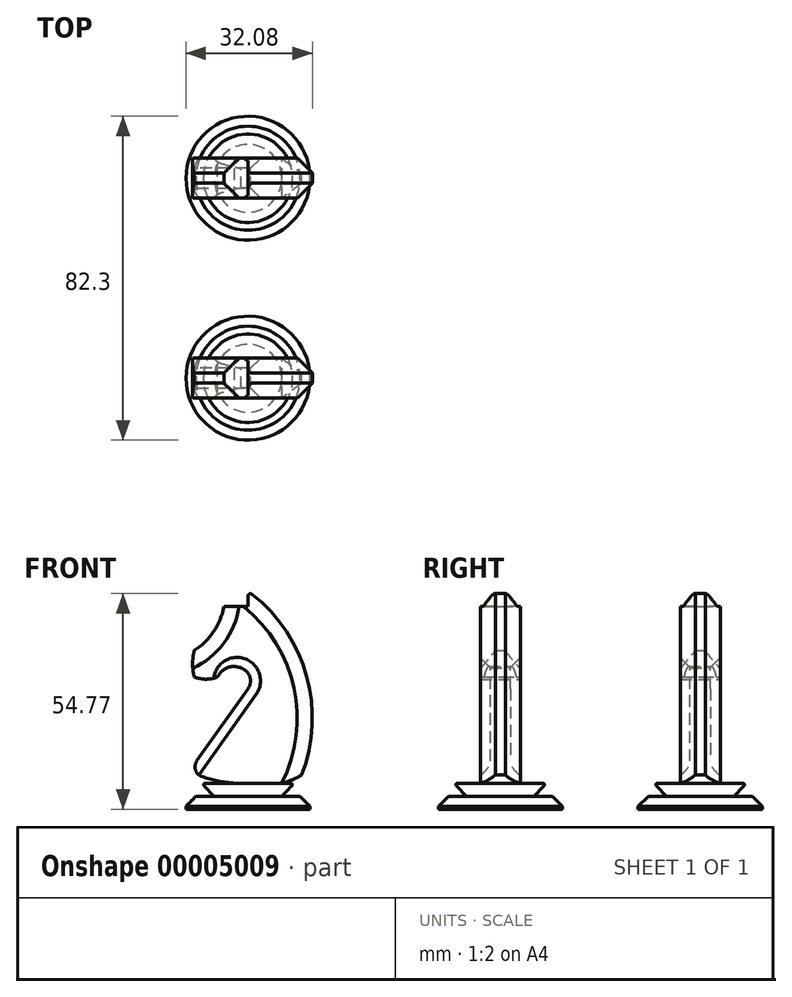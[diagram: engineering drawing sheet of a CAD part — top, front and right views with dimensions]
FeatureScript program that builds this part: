
annotation { "Feature Type Name" : "Feature", "Feature Type Description" : "" }
export const myFeature = defineFeature(function(context is Context, id is Id, definition is map)
    precondition{}
    {
        {
            var Q0;
            Q0=qCreatedBy(makeId("Front.planeOp"),FACE);
            var sketch = newSketch(context, id + "F0", { "sketchPlane" : qUnion([Q0])});
            skLineSegment(sketch, "E0", {"start": v(0, 39.65) * mm, "end": v(0, -18.77) * mm});
            skLineSegment(sketch, "E1", {"start": v(0, -18.77) * mm, "end": v(-15.75, -18.77) * mm});
            skLineSegment(sketch, "E2", {"start": v(-15.75, -18.77) * mm, "end": v(-15.75, -15.47) * mm});
            skLineSegment(sketch, "E3", {"start": v(-15.75, -15.47) * mm, "end": v(-8.61, -15.47) * mm});
            skLineSegment(sketch, "E4", {"start": v(-8.61, -15.47) * mm, "end": v(-11.74, -12.14) * mm});
            skLineSegment(sketch, "E5", {"start": v(-11.74, -12.14) * mm, "end": v(0, -12.14) * mm});
            skSolve(sketch);
        }
        {
            var Q0;
            {var subQ1=sQuery(id+"F0.wireOp",EDGE,"E1");Q0=makeQuery(id+"F0.imprint","IMPRINT",FACE,{"disambiguationData":[TD([[makeQuery(id+"F0.imprint","IMPRINT",EDGE,{"derivedFrom":subQ1}),-1.0]])]});}
            var Q1;
            Q1=sQuery(id+"F0.wireOp",EDGE,"E0");
            revolve(context, id + "F1", {"entities" : qUnion([Q0]), "axis" : qUnion([Q1]), "revolveType" : RevolveType.FULL});
        }
        {
            var Q0;
            Q0=qCreatedBy(makeId("Front.planeOp"),FACE);
            var sketch = newSketch(context, id + "F2", { "sketchPlane" : qUnion([Q0])});
            skLineSegment(sketch, "E6.0", {"start": v(-11.74, -12.14) * mm, "end": v(11.74, -12.14) * mm});
            skArc(sketch, "E7", {"start": v(-14.82, -9.1) * mm, "mid": v(-7.61, -11.6) * mm, "end": v(0, -12.14) * mm});
            skArc(sketch, "E8", {"start": v(0, -12.14) * mm, "mid": v(7.02, -12.47) * mm, "end": v(13.64, -10.09) * mm});
            skLineSegment(sketch, "E9", {"start": v(0, -18.62) * mm, "end": v(0, 42.34) * mm, "construction": true});
            skLineSegment(sketch, "E10", {"start": v(-14.82, -9.1) * mm, "end": v(0, 11.86) * mm});
            skArc(sketch, "E11", {"start": v(13.64, -10.09) * mm, "mid": v(14.73, 15.59) * mm, "end": v(0, 36.65) * mm});
            skArc(sketch, "E12", {"start": v(0, 11.86) * mm, "mid": v(0.46, 14.9) * mm, "end": v(-1.71, 17.09) * mm});
            skArc(sketch, "E13", {"start": v(-1.71, 17.09) * mm, "mid": v(-5.19, 17.22) * mm, "end": v(-7.71, 14.84) * mm});
            skLineSegment(sketch, "E14", {"start": v(-7.71, 14.84) * mm, "end": v(-13.66, 14.84) * mm});
            skLineSegment(sketch, "E15", {"start": v(-13.66, 14.84) * mm, "end": v(-13.66, 21.54) * mm});
            skLineSegment(sketch, "E16", {"start": v(0, 32.71) * mm, "end": v(0, 36.65) * mm});
            skLineSegment(sketch, "E17", {"start": v(0, 32.71) * mm, "end": v(-6.12, 32.71) * mm});
            skArc(sketch, "E18", {"start": v(-13.66, 21.54) * mm, "mid": v(-8.74, 26.35) * mm, "end": v(-6.12, 32.71) * mm});
            skArc(sketch, "E19", {"start": v(-13.66, 14.84) * mm, "mid": v(-10.69, 14.27) * mm, "end": v(-7.71, 14.84) * mm});
            skArc(sketch, "E20", {"start": v(-13.66, 21.54) * mm, "mid": v(-14.06, 18.19) * mm, "end": v(-13.66, 14.84) * mm});
            skArc(sketch, "E21", {"start": v(-6.12, 32.71) * mm, "mid": v(-3.06, 32.41) * mm, "end": v(0, 32.71) * mm});
            skSolve(sketch);
        }
        {
            var Q0;
            {var subQ6=sQuery(id+"F2.wireOp",EDGE,"E10");Q0=makeQuery(id+"F2.imprint","IMPRINT",FACE,{"disambiguationData":[TD([[makeQuery(id+"F2.imprint","IMPRINT",EDGE,{"derivedFrom":subQ6}),-1.0]])]});}
            var Q1;
            Q1=makeQuery(id+"F2.imprint","IMPRINT",FACE,{"disambiguationData":[TD([[makeQuery(id+"F2.imprint","IMPRINT",EDGE,{"derivedFrom":sQuery(id+"F2.wireOp",EDGE,"E14")}),1.0]])]});
            var Q2;
            Q2=makeQuery(id+"F2.imprint","IMPRINT",FACE,{"disambiguationData":[TD([[makeQuery(id+"F2.imprint","IMPRINT",EDGE,{"derivedFrom":sQuery(id+"F2.wireOp",EDGE,"E15")}),1.0]])]});
            var Q3;
            Q3=makeQuery(id+"F2.imprint","IMPRINT",FACE,{"disambiguationData":[TD([[makeQuery(id+"F2.imprint","IMPRINT",EDGE,{"derivedFrom":sQuery(id+"F2.wireOp",EDGE,"E17")}),1.0]])]});
            extrude(context, id + "F3", {"entities" : qUnion([Q0, Q1, Q2, Q3]), "operationType" : NewBodyOperationType.ADD, "endBound" : BoundingType.SYMMETRIC, "depth" : 10.16 * mm});
        }
        {
            var Q0;
            Q0=makeQuery(id+"F3.opExtrude","CAP_EDGE",EDGE,{"disambiguationData":[OSD([sQuery(id+"F2.wireOp",EDGE,"E10")])],"isStart":false});
            var Q1;
            Q1=makeQuery(id+"F3.opExtrude","CAP_EDGE",EDGE,{"disambiguationData":[OSD([sQuery(id+"F2.wireOp",EDGE,"E10")])],"isStart":true});
            chamfer(context, id + "F4", {"entities" : qUnion([Q0, Q1]), "width" : 2.54 * mm, "tangentPropagation" : true});
        }
        {
            var Q0;
            Q0=makeQuery(id+"F3.opExtrude","CAP_EDGE",EDGE,{"disambiguationData":[OSD([sQuery(id+"F2.wireOp",EDGE,"E11")])],"isStart":false});
            var Q1;
            Q1=makeQuery(id+"F3.opExtrude","CAP_EDGE",EDGE,{"disambiguationData":[OSD([sQuery(id+"F2.wireOp",EDGE,"E11")])],"isStart":true});
            chamfer(context, id + "F5", {"entities" : qUnion([Q0, Q1]), "width" : 3.8 * mm, "tangentPropagation" : true});
        }
        {
            var Q0;
            Q0=makeQuery(id+"F3.opExtrude","CAP_EDGE",EDGE,{"disambiguationData":[OSD([sQuery(id+"F2.wireOp",EDGE,"E18")])],"isStart":false});
            var Q1;
            Q1=makeQuery(id+"F3.opExtrude","CAP_EDGE",EDGE,{"disambiguationData":[OSD([sQuery(id+"F2.wireOp",EDGE,"E18")])],"isStart":true});
            chamfer(context, id + "F6", {"entities" : qUnion([Q0, Q1]), "width" : 3.8 * mm, "tangentPropagation" : true});
        }
        {
            var Q0;
            Q0=makeQuery(id+"F1.opRevolve","SWEPT_EDGE",EDGE,{"disambiguationData":[OSD([sQuery(id+"F0.wireOp",EDGE,"E2"),sQuery(id+"F0.wireOp",EDGE,"E3")])]});
            chamfer(context, id + "F7", {"entities" : qUnion([Q0]), "width" : 2.54 * mm, "tangentPropagation" : true});
        }
        {
            var Q0;
            Q0=makeQuery(id+"F3.opExtrude","SWEPT_EDGE",EDGE,{"disambiguationData":[OSD([sQuery(id+"F2.wireOp",EDGE,"E7"),sQuery(id+"F2.wireOp",EDGE,"E10")])]});
            fillet(context, id + "F8", {"entities" : qUnion([Q0]), "radius" : 2.54 * mm, "tangentPropagation" : true, "allowEdgeOverflow" : false});
        }
        {
            var Q0;
            Q0=makeQuery(id+"F1.opRevolve","SWEPT_BODY",BODY,{"disambiguationData":[OSD([sQuery(id+"F0.wireOp",EDGE,"E0"),sQuery(id+"F0.wireOp",EDGE,"E1"),sQuery(id+"F0.wireOp",EDGE,"E2"),sQuery(id+"F0.wireOp",EDGE,"E3"),sQuery(id+"F0.wireOp",EDGE,"E4"),sQuery(id+"F0.wireOp",EDGE,"E5")])]});
            transform(context, id + "F9", {"entities" : qUnion([Q0]), "transformType" : TransformType.TRANSLATION_3D, "dx" : 0 * mm, "dy" : 50.8 * mm, "dz" : 0 * mm, "makeCopy" : true});
        }
        {
            var Q0;
            Q0=makeQuery(id+"F1.opRevolve","SWEPT_EDGE",EDGE,{"disambiguationData":[OSD([sQuery(id+"F0.wireOp",EDGE,"E4"),sQuery(id+"F0.wireOp",EDGE,"E5")])]});
            var Q1;
            Q1=makeQuery(id+"F9.opPattern","COPY",EDGE,{"derivedFrom":makeQuery(id+"F1.opRevolve","SWEPT_EDGE",EDGE,{"disambiguationData":[OSD([sQuery(id+"F0.wireOp",EDGE,"E4"),sQuery(id+"F0.wireOp",EDGE,"E5")])]}),"instanceName":"1"});
            fillet(context, id + "F10", {"entities" : qUnion([Q0, Q1]), "radius" : 0.38 * mm, "tangentPropagation" : true, "allowEdgeOverflow" : false});
        }
        {
            var Q0;
            Q0=makeQuery(id+"F3.opExtrude","SWEPT_EDGE",EDGE,{"disambiguationData":[OSD([sQuery(id+"F2.wireOp",EDGE,"E11"),sQuery(id+"F2.wireOp",EDGE,"E16")])]});
            var Q1;
            Q1=makeQuery(id+"F9.opPattern","COPY",EDGE,{"derivedFrom":makeQuery(id+"F3.opExtrude","SWEPT_EDGE",EDGE,{"disambiguationData":[OSD([sQuery(id+"F2.wireOp",EDGE,"E11"),sQuery(id+"F2.wireOp",EDGE,"E16")])]}),"instanceName":"1"});
            fillet(context, id + "F11", {"entities" : qUnion([Q0, Q1]), "radius" : 0.64 * mm, "tangentPropagation" : true, "allowEdgeOverflow" : false});
        }
    });
